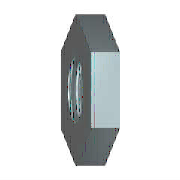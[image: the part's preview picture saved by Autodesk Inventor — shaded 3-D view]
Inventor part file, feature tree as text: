
AUTODESK INVENTOR PART (.ipt)
format: ipt  version: 2022 (Build 260153000, 153)  size: 136,192 bytes
history: native  units: mm (DEFAULTED — no unit token found)
features: other x4, sketch x2
ambient origin geometry x8: Origin, YZ Plane, XZ Plane, XY Plane, X Axis, Y Axis, Z Axis, Center Point
bodies: Solid1 (feature_tree)
feature tree (6):
  other  "MSC_A1"
  other  "MSC_PT1"
  other  "MSC_PT2"
  other  "MSC_PF1"
  sketch  "Boceto1"  dims[d2=0.0mm]
  sketch  "Boceto2"  dims[d3=2.459mm d4=1.8mm d5=4.0mm d6=2.0mm d7=60.0deg d8=8.0mm d9=20.594885mm d14=0.0mm d15=0.0mm d16=0.0mm d17=0.3mm d18=0.3mm d20=45.0deg d21=0.0mm d23=0.0mm d24=0.0mm d25=0.0mm]
